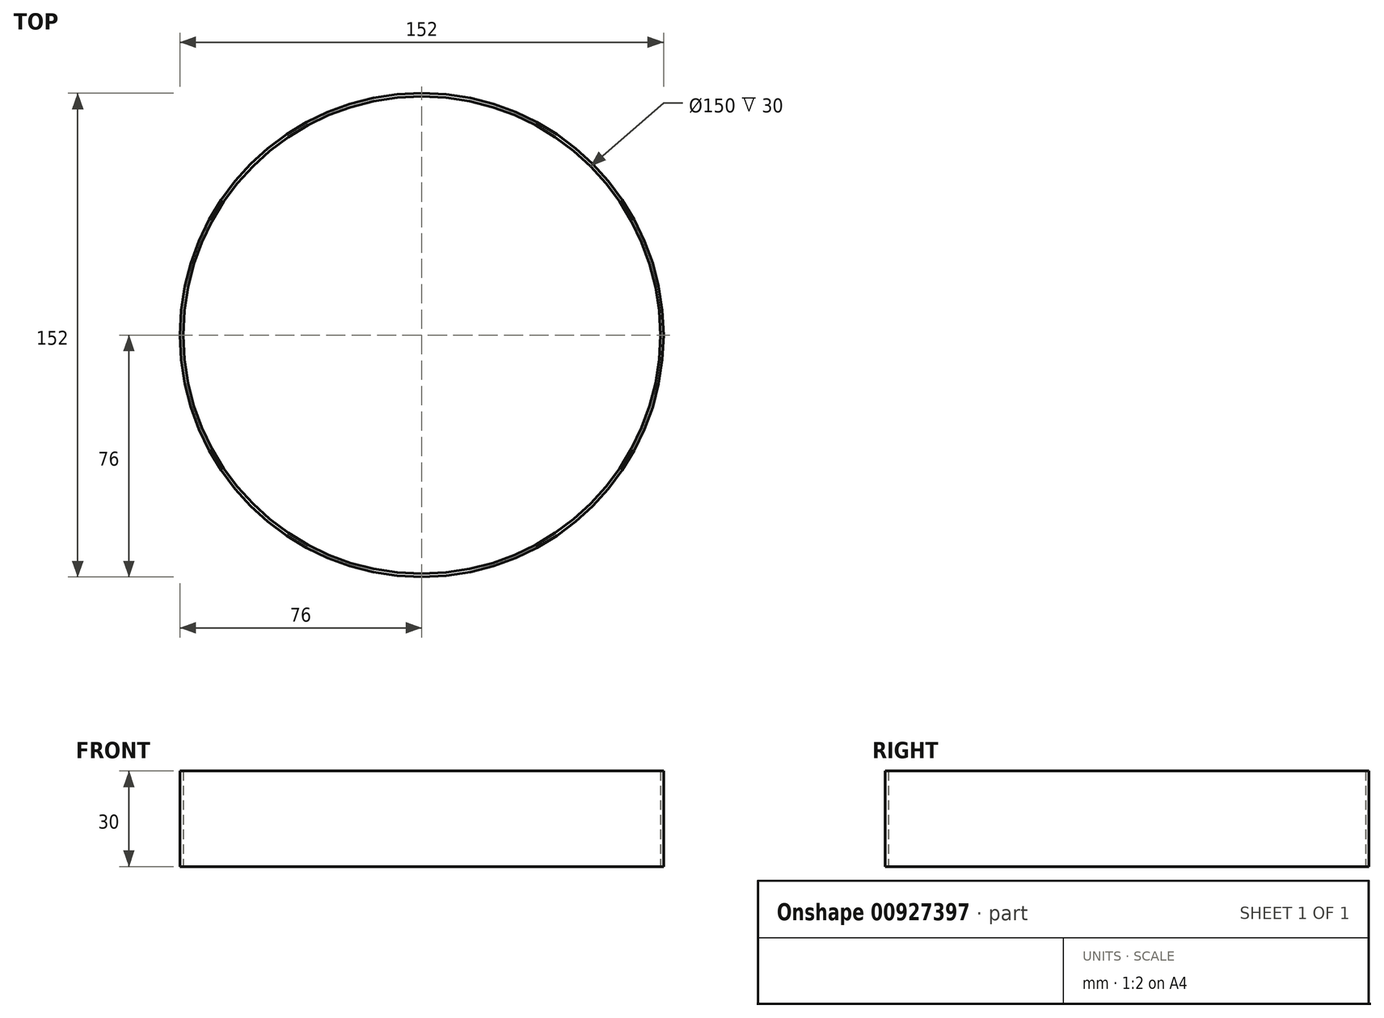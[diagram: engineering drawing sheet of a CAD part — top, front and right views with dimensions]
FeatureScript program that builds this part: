
annotation { "Feature Type Name" : "Feature", "Feature Type Description" : "" }
export const myFeature = defineFeature(function(context is Context, id is Id, definition is map)
    precondition{}
    {
        {
            var Q0;
            Q0=qCreatedBy(makeId("Top.planeOp"),FACE);
            var sketch = newSketch(context, id + "F0", { "sketchPlane" : qUnion([Q0])});
            skCircle(sketch, "E0", {"center": v(0, 0) * mm, "radius": 75 * mm});
            skCircle(sketch, "E1.0", {"center": v(0, 0) * mm, "radius": 76 * mm});
            skSolve(sketch);
        }
        {
            var Q0;
            Q0 = qSketchRegion(id + "F0", true);
            extrude(context, id + "F1", {"entities" : qUnion([Q0]), "depth" : 30 * mm, "offsetDistance" : 25 * mm});
        }
    });
